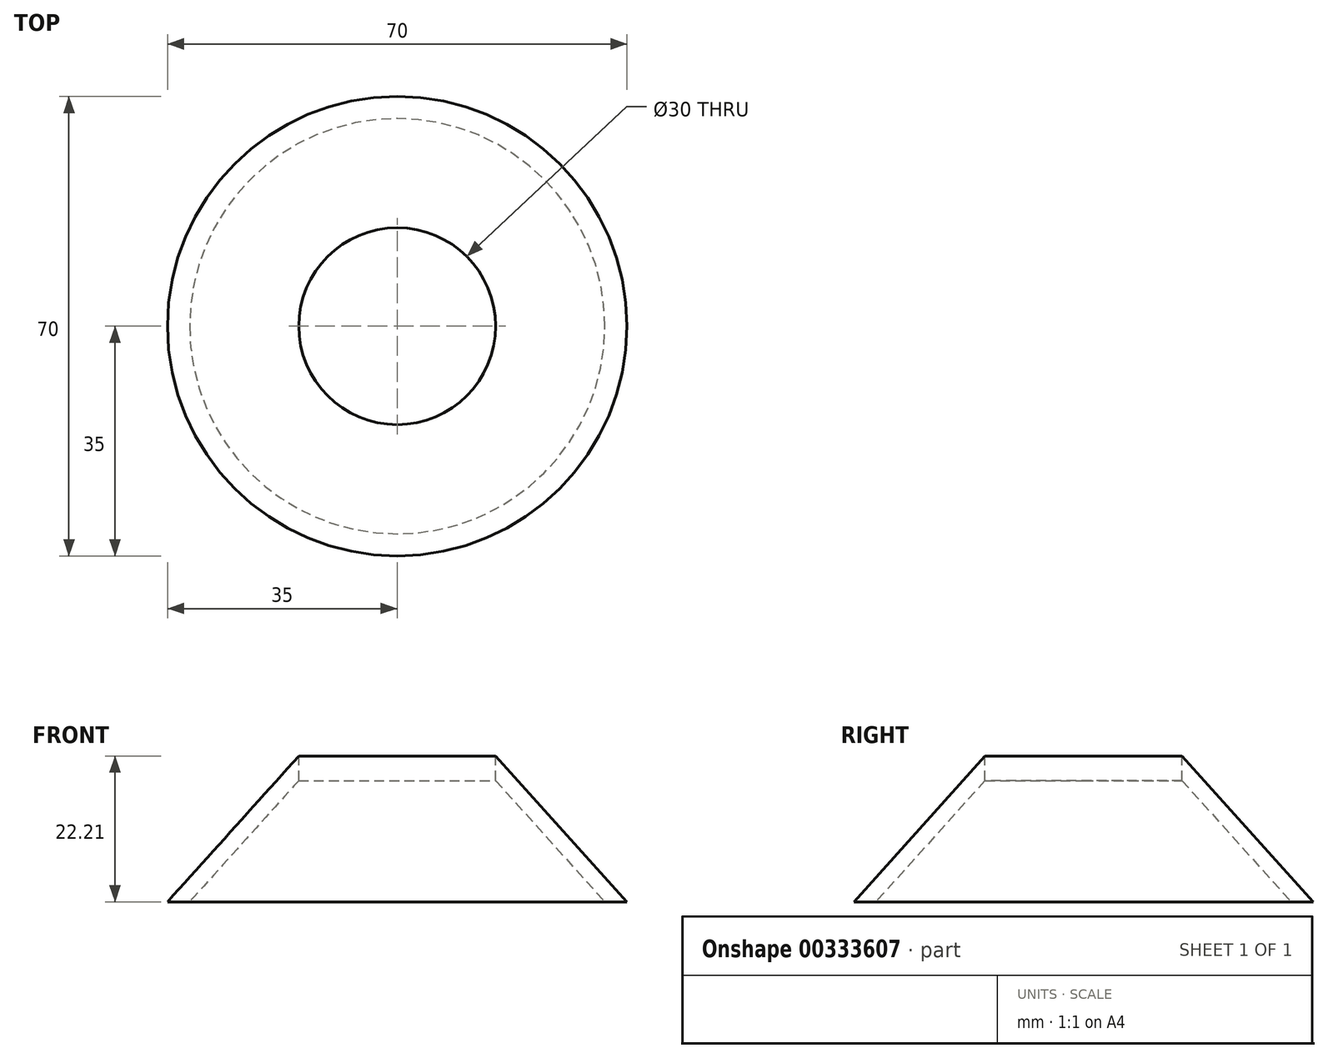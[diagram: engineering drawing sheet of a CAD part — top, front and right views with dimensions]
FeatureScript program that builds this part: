
annotation { "Feature Type Name" : "Feature", "Feature Type Description" : "" }
export const myFeature = defineFeature(function(context is Context, id is Id, definition is map)
    precondition{}
    {
        {
            var Q0;
            Q0=qCreatedBy(makeId("Front.planeOp"),FACE);
            var sketch = newSketch(context, id + "F0", { "sketchPlane" : qUnion([Q0])});
            skLineSegment(sketch, "E0", {"start": v(0, 22.21) * mm, "end": v(-15, 22.21) * mm});
            skLineSegment(sketch, "E1", {"start": v(-15, 22.21) * mm, "end": v(-35, 0) * mm});
            skLineSegment(sketch, "E2", {"start": v(-35, 0) * mm, "end": v(0, 0) * mm});
            skLineSegment(sketch, "E3", {"start": v(0, 0) * mm, "end": v(0, 22.21) * mm});
            skLineSegment(sketch, "E4", {"start": v(0, 22.21) * mm, "end": v(0, 39.2) * mm, "construction": true});
            skSolve(sketch);
        }
        {
            var Q0;
            Q0=makeQuery(id+"F0.imprint","IMPRINT",FACE,{"disambiguationData":[TD([[makeQuery(id+"F0.imprint","IMPRINT",EDGE,{"derivedFrom":sQuery(id+"F0.wireOp",EDGE,"E0")}),1.0]])]});
            var Q1;
            Q1=sQuery(id+"F0.wireOp",EDGE,"E4");
            revolve(context, id + "F1", {"entities" : qUnion([Q0]), "axis" : qUnion([Q1]), "revolveType" : RevolveType.FULL});
        }
        {
            var Q0;
            Q0=makeQuery(id+"F1.opRevolve","SWEPT_FACE",FACE,{"disambiguationData":[OSD([sQuery(id+"F0.wireOp",EDGE,"E2")])]});
            shell(context, id + "F2", {"entities" : qUnion([Q0]), "thickness" : 2.5 * mm});
        }
        {
            var Q0;
            Q0=makeQuery(id+"F1.opRevolve","SWEPT_FACE",FACE,{"disambiguationData":[OSD([sQuery(id+"F0.wireOp",EDGE,"E0")])]});
            extrude(context, id + "F3", {"entities" : qUnion([Q0]), "operationType" : NewBodyOperationType.REMOVE, "oppositeDirection" : true, "depth" : 25 * mm});
        }
    });
